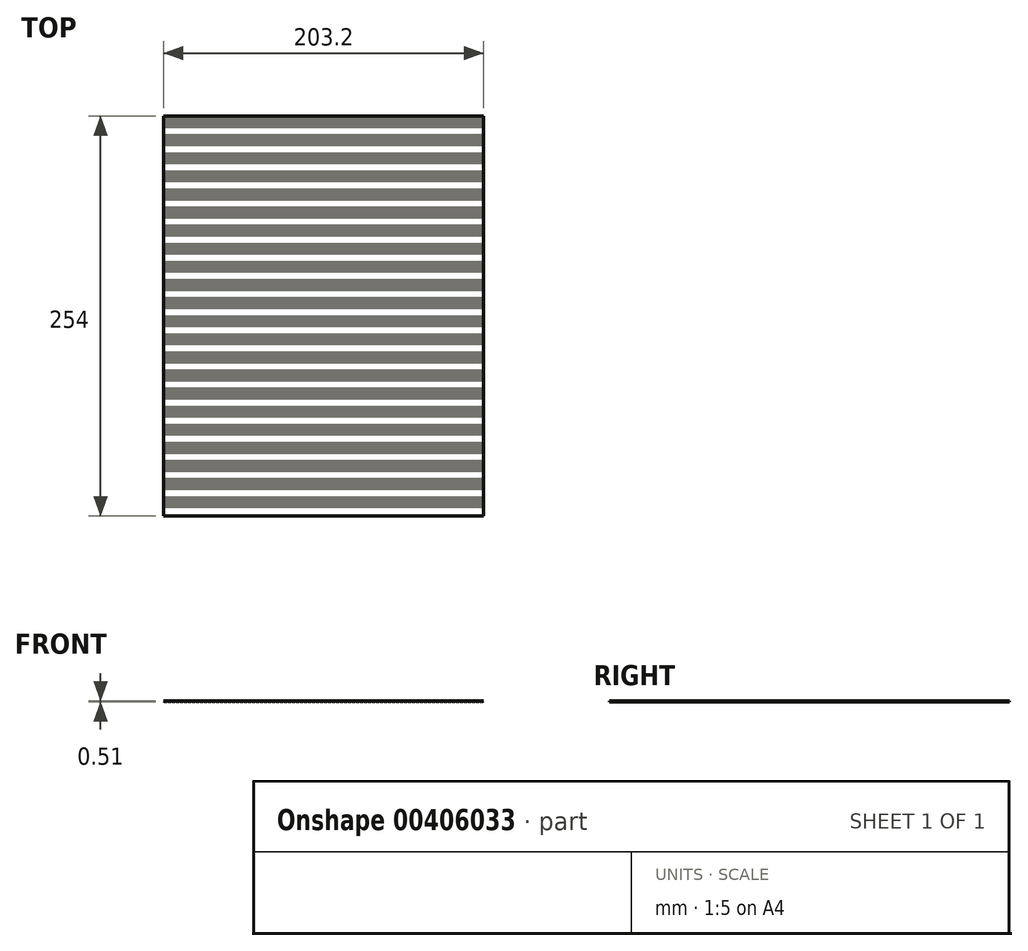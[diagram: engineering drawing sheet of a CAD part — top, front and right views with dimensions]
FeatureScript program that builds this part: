
annotation { "Feature Type Name" : "Feature", "Feature Type Description" : "" }
export const myFeature = defineFeature(function(context is Context, id is Id, definition is map)
    precondition{}
    {
        {
            var Q0;
            Q0=qCreatedBy(makeId("Front.planeOp"),FACE);
            var sketch = newSketch(context, id + "F0", { "sketchPlane" : qUnion([Q0])});
            skLineSegment(sketch, "E0", {"start": v(0, 0) * mm, "end": v(-1.27, -0.5) * mm});
            skLineSegment(sketch, "E1", {"start": v(-1.27, -0.5) * mm, "end": v(-2.54, 0) * mm});
            skLineSegment(sketch, "E2", {"start": v(0, 0) * mm, "end": v(-2.54, 0) * mm, "construction": true});
            skLineSegment(sketch, "E3.1.0.0", {"start": v(-3.8, -0.5) * mm, "end": v(-5.08, 0) * mm});
            skLineSegment(sketch, "E3.1.0.1", {"start": v(-2.54, 0) * mm, "end": v(-3.81, -0.5) * mm});
            skLineSegment(sketch, "E3.1.0.2", {"start": v(-2.54, 0) * mm, "end": v(-5.08, 0) * mm, "construction": true});
            skLineSegment(sketch, "E3.2.0.0", {"start": v(-6.35, -0.5) * mm, "end": v(-7.62, 0) * mm});
            skLineSegment(sketch, "E3.2.0.1", {"start": v(-5.08, 0) * mm, "end": v(-6.35, -0.5) * mm});
            skLineSegment(sketch, "E3.2.0.2", {"start": v(-5.08, 0) * mm, "end": v(-7.62, 0) * mm, "construction": true});
            skLineSegment(sketch, "E3.direction1", {"start": v(-2.54, 0) * mm, "end": v(-5.08, 0) * mm, "construction": true});
            skLineSegment(sketch, "E4.0.3.0", {"start": v(-8.89, -0.5) * mm, "end": v(-10.16, 0) * mm});
            skLineSegment(sketch, "E4.3.3.0", {"start": v(-7.62, 0) * mm, "end": v(-8.89, -0.5) * mm});
            skLineSegment(sketch, "E4.6.3.0", {"start": v(-7.62, 0) * mm, "end": v(-10.16, 0) * mm, "construction": true});
            skLineSegment(sketch, "E4.0.4.0", {"start": v(-11.43, -0.5) * mm, "end": v(-12.7, 0) * mm});
            skLineSegment(sketch, "E4.3.4.0", {"start": v(-10.16, 0) * mm, "end": v(-11.43, -0.5) * mm});
            skLineSegment(sketch, "E4.6.4.0", {"start": v(-10.16, 0) * mm, "end": v(-12.7, 0) * mm, "construction": true});
            skLineSegment(sketch, "E4.0.5.0", {"start": v(-13.97, -0.5) * mm, "end": v(-15.24, 0) * mm});
            skLineSegment(sketch, "E4.3.5.0", {"start": v(-12.7, 0) * mm, "end": v(-13.97, -0.5) * mm});
            skLineSegment(sketch, "E4.6.5.0", {"start": v(-12.7, 0) * mm, "end": v(-15.24, 0) * mm, "construction": true});
            skLineSegment(sketch, "E4.0.6.0", {"start": v(-16.5, -0.5) * mm, "end": v(-17.78, 0) * mm});
            skLineSegment(sketch, "E4.3.6.0", {"start": v(-15.24, 0) * mm, "end": v(-16.5, -0.5) * mm});
            skLineSegment(sketch, "E4.6.6.0", {"start": v(-15.24, 0) * mm, "end": v(-17.78, 0) * mm, "construction": true});
            skLineSegment(sketch, "E4.0.7.0", {"start": v(-19.05, -0.5) * mm, "end": v(-20.32, 0) * mm});
            skLineSegment(sketch, "E4.3.7.0", {"start": v(-17.78, 0) * mm, "end": v(-19.05, -0.5) * mm});
            skLineSegment(sketch, "E4.6.7.0", {"start": v(-17.78, 0) * mm, "end": v(-20.32, 0) * mm, "construction": true});
            skLineSegment(sketch, "E4.0.8.0", {"start": v(-21.59, -0.5) * mm, "end": v(-22.86, 0) * mm});
            skLineSegment(sketch, "E4.3.8.0", {"start": v(-20.32, 0) * mm, "end": v(-21.59, -0.5) * mm});
            skLineSegment(sketch, "E4.6.8.0", {"start": v(-20.32, 0) * mm, "end": v(-22.86, 0) * mm, "construction": true});
            skLineSegment(sketch, "E4.0.9.0", {"start": v(-24.13, -0.5) * mm, "end": v(-25.4, 0) * mm});
            skLineSegment(sketch, "E4.3.9.0", {"start": v(-22.86, 0) * mm, "end": v(-24.13, -0.5) * mm});
            skLineSegment(sketch, "E4.6.9.0", {"start": v(-22.86, 0) * mm, "end": v(-25.4, 0) * mm, "construction": true});
            skLineSegment(sketch, "E4.0.10.0", {"start": v(-26.67, -0.5) * mm, "end": v(-27.94, 0) * mm});
            skLineSegment(sketch, "E4.3.10.0", {"start": v(-25.4, 0) * mm, "end": v(-26.67, -0.5) * mm});
            skLineSegment(sketch, "E4.6.10.0", {"start": v(-25.4, 0) * mm, "end": v(-27.94, 0) * mm, "construction": true});
            skLineSegment(sketch, "E4.0.11.0", {"start": v(-29.2, -0.5) * mm, "end": v(-30.48, 0) * mm});
            skLineSegment(sketch, "E4.3.11.0", {"start": v(-27.94, 0) * mm, "end": v(-29.21, -0.5) * mm});
            skLineSegment(sketch, "E4.6.11.0", {"start": v(-27.94, 0) * mm, "end": v(-30.48, 0) * mm, "construction": true});
            skLineSegment(sketch, "E4.0.12.0", {"start": v(-31.75, -0.5) * mm, "end": v(-33.02, 0) * mm});
            skLineSegment(sketch, "E4.3.12.0", {"start": v(-30.48, 0) * mm, "end": v(-31.75, -0.5) * mm});
            skLineSegment(sketch, "E4.6.12.0", {"start": v(-30.48, 0) * mm, "end": v(-33.02, 0) * mm, "construction": true});
            skLineSegment(sketch, "E4.0.13.0", {"start": v(-34.3, -0.5) * mm, "end": v(-35.56, 0) * mm});
            skLineSegment(sketch, "E4.3.13.0", {"start": v(-33.02, 0) * mm, "end": v(-34.29, -0.5) * mm});
            skLineSegment(sketch, "E4.6.13.0", {"start": v(-33.02, 0) * mm, "end": v(-35.56, 0) * mm, "construction": true});
            skLineSegment(sketch, "E4.0.14.0", {"start": v(-36.83, -0.5) * mm, "end": v(-38.1, 0) * mm});
            skLineSegment(sketch, "E4.3.14.0", {"start": v(-35.56, 0) * mm, "end": v(-36.83, -0.5) * mm});
            skLineSegment(sketch, "E4.6.14.0", {"start": v(-35.56, 0) * mm, "end": v(-38.1, 0) * mm, "construction": true});
            skLineSegment(sketch, "E4.0.15.0", {"start": v(-39.37, -0.5) * mm, "end": v(-40.64, 0) * mm});
            skLineSegment(sketch, "E4.3.15.0", {"start": v(-38.1, 0) * mm, "end": v(-39.37, -0.5) * mm});
            skLineSegment(sketch, "E4.6.15.0", {"start": v(-38.1, 0) * mm, "end": v(-40.64, 0) * mm, "construction": true});
            skLineSegment(sketch, "E4.0.16.0", {"start": v(-41.9, -0.5) * mm, "end": v(-43.18, 0) * mm});
            skLineSegment(sketch, "E4.3.16.0", {"start": v(-40.64, 0) * mm, "end": v(-41.9, -0.5) * mm});
            skLineSegment(sketch, "E4.6.16.0", {"start": v(-40.64, 0) * mm, "end": v(-43.18, 0) * mm, "construction": true});
            skLineSegment(sketch, "E4.0.17.0", {"start": v(-44.45, -0.5) * mm, "end": v(-45.72, 0) * mm});
            skLineSegment(sketch, "E4.3.17.0", {"start": v(-43.18, 0) * mm, "end": v(-44.45, -0.5) * mm});
            skLineSegment(sketch, "E4.6.17.0", {"start": v(-43.18, 0) * mm, "end": v(-45.72, 0) * mm, "construction": true});
            skLineSegment(sketch, "E4.0.18.0", {"start": v(-46.99, -0.5) * mm, "end": v(-48.26, 0) * mm});
            skLineSegment(sketch, "E4.3.18.0", {"start": v(-45.72, 0) * mm, "end": v(-46.99, -0.5) * mm});
            skLineSegment(sketch, "E4.6.18.0", {"start": v(-45.72, 0) * mm, "end": v(-48.26, 0) * mm, "construction": true});
            skLineSegment(sketch, "E4.0.19.0", {"start": v(-49.53, -0.5) * mm, "end": v(-50.8, 0) * mm});
            skLineSegment(sketch, "E4.3.19.0", {"start": v(-48.26, 0) * mm, "end": v(-49.53, -0.5) * mm});
            skLineSegment(sketch, "E4.6.19.0", {"start": v(-48.26, 0) * mm, "end": v(-50.8, 0) * mm, "construction": true});
            skLineSegment(sketch, "E4.0.20.0", {"start": v(-52.07, -0.5) * mm, "end": v(-53.34, 0) * mm});
            skLineSegment(sketch, "E4.3.20.0", {"start": v(-50.8, 0) * mm, "end": v(-52.07, -0.5) * mm});
            skLineSegment(sketch, "E4.6.20.0", {"start": v(-50.8, 0) * mm, "end": v(-53.34, 0) * mm, "construction": true});
            skLineSegment(sketch, "E4.0.21.0", {"start": v(-54.6, -0.5) * mm, "end": v(-55.88, 0) * mm});
            skLineSegment(sketch, "E4.3.21.0", {"start": v(-53.34, 0) * mm, "end": v(-54.61, -0.5) * mm});
            skLineSegment(sketch, "E4.6.21.0", {"start": v(-53.34, 0) * mm, "end": v(-55.88, 0) * mm, "construction": true});
            skLineSegment(sketch, "E4.0.22.0", {"start": v(-57.15, -0.5) * mm, "end": v(-58.42, 0) * mm});
            skLineSegment(sketch, "E4.3.22.0", {"start": v(-55.88, 0) * mm, "end": v(-57.15, -0.5) * mm});
            skLineSegment(sketch, "E4.6.22.0", {"start": v(-55.88, 0) * mm, "end": v(-58.42, 0) * mm, "construction": true});
            skLineSegment(sketch, "E4.0.23.0", {"start": v(-59.69, -0.5) * mm, "end": v(-60.96, 0) * mm});
            skLineSegment(sketch, "E4.3.23.0", {"start": v(-58.42, 0) * mm, "end": v(-59.69, -0.5) * mm});
            skLineSegment(sketch, "E4.6.23.0", {"start": v(-58.42, 0) * mm, "end": v(-60.96, 0) * mm, "construction": true});
            skLineSegment(sketch, "E4.0.24.0", {"start": v(-62.23, -0.5) * mm, "end": v(-63.5, 0) * mm});
            skLineSegment(sketch, "E4.3.24.0", {"start": v(-60.96, 0) * mm, "end": v(-62.23, -0.5) * mm});
            skLineSegment(sketch, "E4.6.24.0", {"start": v(-60.96, 0) * mm, "end": v(-63.5, 0) * mm, "construction": true});
            skLineSegment(sketch, "E4.0.25.0", {"start": v(-64.77, -0.5) * mm, "end": v(-66.04, 0) * mm});
            skLineSegment(sketch, "E4.3.25.0", {"start": v(-63.5, 0) * mm, "end": v(-64.77, -0.5) * mm});
            skLineSegment(sketch, "E4.6.25.0", {"start": v(-63.5, 0) * mm, "end": v(-66.04, 0) * mm, "construction": true});
            skLineSegment(sketch, "E4.0.26.0", {"start": v(-67.31, -0.5) * mm, "end": v(-68.58, 0) * mm});
            skLineSegment(sketch, "E4.3.26.0", {"start": v(-66.04, 0) * mm, "end": v(-67.3, -0.5) * mm});
            skLineSegment(sketch, "E4.6.26.0", {"start": v(-66.04, 0) * mm, "end": v(-68.58, 0) * mm, "construction": true});
            skLineSegment(sketch, "E4.0.27.0", {"start": v(-69.85, -0.5) * mm, "end": v(-71.12, 0) * mm});
            skLineSegment(sketch, "E4.3.27.0", {"start": v(-68.58, 0) * mm, "end": v(-69.85, -0.5) * mm});
            skLineSegment(sketch, "E4.6.27.0", {"start": v(-68.58, 0) * mm, "end": v(-71.12, 0) * mm, "construction": true});
            skLineSegment(sketch, "E4.0.28.0", {"start": v(-72.39, -0.5) * mm, "end": v(-73.66, 0) * mm});
            skLineSegment(sketch, "E4.3.28.0", {"start": v(-71.12, 0) * mm, "end": v(-72.39, -0.5) * mm});
            skLineSegment(sketch, "E4.6.28.0", {"start": v(-71.12, 0) * mm, "end": v(-73.66, 0) * mm, "construction": true});
            skLineSegment(sketch, "E4.0.29.0", {"start": v(-74.93, -0.5) * mm, "end": v(-76.2, 0) * mm});
            skLineSegment(sketch, "E4.3.29.0", {"start": v(-73.66, 0) * mm, "end": v(-74.93, -0.5) * mm});
            skLineSegment(sketch, "E4.6.29.0", {"start": v(-73.66, 0) * mm, "end": v(-76.2, 0) * mm, "construction": true});
            skLineSegment(sketch, "E4.0.30.0", {"start": v(-77.47, -0.5) * mm, "end": v(-78.74, 0) * mm});
            skLineSegment(sketch, "E4.3.30.0", {"start": v(-76.2, 0) * mm, "end": v(-77.47, -0.5) * mm});
            skLineSegment(sketch, "E4.6.30.0", {"start": v(-76.2, 0) * mm, "end": v(-78.74, 0) * mm, "construction": true});
            skLineSegment(sketch, "E4.0.31.0", {"start": v(-80, -0.5) * mm, "end": v(-81.28, 0) * mm});
            skLineSegment(sketch, "E4.3.31.0", {"start": v(-78.74, 0) * mm, "end": v(-80, -0.5) * mm});
            skLineSegment(sketch, "E4.6.31.0", {"start": v(-78.74, 0) * mm, "end": v(-81.28, 0) * mm, "construction": true});
            skLineSegment(sketch, "E4.0.32.0", {"start": v(-82.55, -0.5) * mm, "end": v(-83.82, 0) * mm});
            skLineSegment(sketch, "E4.3.32.0", {"start": v(-81.28, 0) * mm, "end": v(-82.55, -0.5) * mm});
            skLineSegment(sketch, "E4.6.32.0", {"start": v(-81.28, 0) * mm, "end": v(-83.82, 0) * mm, "construction": true});
            skLineSegment(sketch, "E4.0.33.0", {"start": v(-85.1, -0.5) * mm, "end": v(-86.36, 0) * mm});
            skLineSegment(sketch, "E4.3.33.0", {"start": v(-83.82, 0) * mm, "end": v(-85.1, -0.5) * mm});
            skLineSegment(sketch, "E4.6.33.0", {"start": v(-83.82, 0) * mm, "end": v(-86.36, 0) * mm, "construction": true});
            skLineSegment(sketch, "E4.0.34.0", {"start": v(-87.63, -0.5) * mm, "end": v(-88.9, 0) * mm});
            skLineSegment(sketch, "E4.3.34.0", {"start": v(-86.36, 0) * mm, "end": v(-87.63, -0.5) * mm});
            skLineSegment(sketch, "E4.6.34.0", {"start": v(-86.36, 0) * mm, "end": v(-88.9, 0) * mm, "construction": true});
            skLineSegment(sketch, "E4.0.35.0", {"start": v(-90.17, -0.5) * mm, "end": v(-91.44, 0) * mm});
            skLineSegment(sketch, "E4.3.35.0", {"start": v(-88.9, 0) * mm, "end": v(-90.17, -0.5) * mm});
            skLineSegment(sketch, "E4.6.35.0", {"start": v(-88.9, 0) * mm, "end": v(-91.44, 0) * mm, "construction": true});
            skLineSegment(sketch, "E4.0.36.0", {"start": v(-92.7, -0.5) * mm, "end": v(-93.98, 0) * mm});
            skLineSegment(sketch, "E4.3.36.0", {"start": v(-91.44, 0) * mm, "end": v(-92.7, -0.5) * mm});
            skLineSegment(sketch, "E4.6.36.0", {"start": v(-91.44, 0) * mm, "end": v(-93.98, 0) * mm, "construction": true});
            skLineSegment(sketch, "E4.0.37.0", {"start": v(-95.25, -0.5) * mm, "end": v(-96.52, 0) * mm});
            skLineSegment(sketch, "E4.3.37.0", {"start": v(-93.98, 0) * mm, "end": v(-95.25, -0.5) * mm});
            skLineSegment(sketch, "E4.6.37.0", {"start": v(-93.98, 0) * mm, "end": v(-96.52, 0) * mm, "construction": true});
            skLineSegment(sketch, "E4.0.38.0", {"start": v(-97.79, -0.5) * mm, "end": v(-99.06, 0) * mm});
            skLineSegment(sketch, "E4.3.38.0", {"start": v(-96.52, 0) * mm, "end": v(-97.8, -0.5) * mm});
            skLineSegment(sketch, "E4.6.38.0", {"start": v(-96.52, 0) * mm, "end": v(-99.06, 0) * mm, "construction": true});
            skLineSegment(sketch, "E4.0.39.0", {"start": v(-100.33, -0.5) * mm, "end": v(-101.6, 0) * mm});
            skLineSegment(sketch, "E4.3.39.0", {"start": v(-99.06, 0) * mm, "end": v(-100.33, -0.5) * mm});
            skLineSegment(sketch, "E4.6.39.0", {"start": v(-99.06, 0) * mm, "end": v(-101.6, 0) * mm, "construction": true});
            skLineSegment(sketch, "E5", {"start": v(0, 0) * mm, "end": v(0, 0) * mm});
            skLineSegment(sketch, "E6", {"start": v(0, 0) * mm, "end": v(-203.2, 0) * mm});
            skLineSegment(sketch, "E7.0.40.0", {"start": v(-102.87, -0.5) * mm, "end": v(-104.14, 0) * mm});
            skLineSegment(sketch, "E7.3.40.0", {"start": v(-101.6, 0) * mm, "end": v(-102.87, -0.5) * mm});
            skLineSegment(sketch, "E7.6.40.0", {"start": v(-101.6, 0) * mm, "end": v(-104.14, 0) * mm, "construction": true});
            skLineSegment(sketch, "E7.0.41.0", {"start": v(-105.41, -0.5) * mm, "end": v(-106.68, 0) * mm});
            skLineSegment(sketch, "E7.3.41.0", {"start": v(-104.14, 0) * mm, "end": v(-105.41, -0.5) * mm});
            skLineSegment(sketch, "E7.6.41.0", {"start": v(-104.14, 0) * mm, "end": v(-106.68, 0) * mm, "construction": true});
            skLineSegment(sketch, "E7.0.42.0", {"start": v(-107.95, -0.5) * mm, "end": v(-109.22, 0) * mm});
            skLineSegment(sketch, "E7.3.42.0", {"start": v(-106.68, 0) * mm, "end": v(-107.95, -0.5) * mm});
            skLineSegment(sketch, "E7.6.42.0", {"start": v(-106.68, 0) * mm, "end": v(-109.22, 0) * mm, "construction": true});
            skLineSegment(sketch, "E7.0.43.0", {"start": v(-110.5, -0.5) * mm, "end": v(-111.76, 0) * mm});
            skLineSegment(sketch, "E7.3.43.0", {"start": v(-109.22, 0) * mm, "end": v(-110.5, -0.5) * mm});
            skLineSegment(sketch, "E7.6.43.0", {"start": v(-109.22, 0) * mm, "end": v(-111.76, 0) * mm, "construction": true});
            skLineSegment(sketch, "E7.0.44.0", {"start": v(-113.03, -0.5) * mm, "end": v(-114.3, 0) * mm});
            skLineSegment(sketch, "E7.3.44.0", {"start": v(-111.76, 0) * mm, "end": v(-113.03, -0.5) * mm});
            skLineSegment(sketch, "E7.6.44.0", {"start": v(-111.76, 0) * mm, "end": v(-114.3, 0) * mm, "construction": true});
            skLineSegment(sketch, "E7.0.45.0", {"start": v(-115.57, -0.5) * mm, "end": v(-116.84, 0) * mm});
            skLineSegment(sketch, "E7.3.45.0", {"start": v(-114.3, 0) * mm, "end": v(-115.57, -0.5) * mm});
            skLineSegment(sketch, "E7.6.45.0", {"start": v(-114.3, 0) * mm, "end": v(-116.84, 0) * mm, "construction": true});
            skLineSegment(sketch, "E7.0.46.0", {"start": v(-118.11, -0.5) * mm, "end": v(-119.38, 0) * mm});
            skLineSegment(sketch, "E7.3.46.0", {"start": v(-116.84, 0) * mm, "end": v(-118.11, -0.5) * mm});
            skLineSegment(sketch, "E7.6.46.0", {"start": v(-116.84, 0) * mm, "end": v(-119.38, 0) * mm, "construction": true});
            skLineSegment(sketch, "E7.0.47.0", {"start": v(-120.65, -0.5) * mm, "end": v(-121.92, 0) * mm});
            skLineSegment(sketch, "E7.3.47.0", {"start": v(-119.38, 0) * mm, "end": v(-120.65, -0.5) * mm});
            skLineSegment(sketch, "E7.6.47.0", {"start": v(-119.38, 0) * mm, "end": v(-121.92, 0) * mm, "construction": true});
            skLineSegment(sketch, "E7.0.48.0", {"start": v(-123.2, -0.5) * mm, "end": v(-124.46, 0) * mm});
            skLineSegment(sketch, "E7.3.48.0", {"start": v(-121.92, 0) * mm, "end": v(-123.19, -0.5) * mm});
            skLineSegment(sketch, "E7.6.48.0", {"start": v(-121.92, 0) * mm, "end": v(-124.46, 0) * mm, "construction": true});
            skLineSegment(sketch, "E7.0.49.0", {"start": v(-125.73, -0.5) * mm, "end": v(-127, 0) * mm});
            skLineSegment(sketch, "E7.3.49.0", {"start": v(-124.46, 0) * mm, "end": v(-125.73, -0.5) * mm});
            skLineSegment(sketch, "E7.6.49.0", {"start": v(-124.46, 0) * mm, "end": v(-127, 0) * mm, "construction": true});
            skLineSegment(sketch, "E7.0.50.0", {"start": v(-128.27, -0.5) * mm, "end": v(-129.54, 0) * mm});
            skLineSegment(sketch, "E7.3.50.0", {"start": v(-127, 0) * mm, "end": v(-128.27, -0.5) * mm});
            skLineSegment(sketch, "E7.6.50.0", {"start": v(-127, 0) * mm, "end": v(-129.54, 0) * mm, "construction": true});
            skLineSegment(sketch, "E7.0.51.0", {"start": v(-130.81, -0.5) * mm, "end": v(-132.08, 0) * mm});
            skLineSegment(sketch, "E7.3.51.0", {"start": v(-129.54, 0) * mm, "end": v(-130.81, -0.5) * mm});
            skLineSegment(sketch, "E7.6.51.0", {"start": v(-129.54, 0) * mm, "end": v(-132.08, 0) * mm, "construction": true});
            skLineSegment(sketch, "E7.0.52.0", {"start": v(-133.35, -0.5) * mm, "end": v(-134.62, 0) * mm});
            skLineSegment(sketch, "E7.3.52.0", {"start": v(-132.08, 0) * mm, "end": v(-133.35, -0.5) * mm});
            skLineSegment(sketch, "E7.6.52.0", {"start": v(-132.08, 0) * mm, "end": v(-134.62, 0) * mm, "construction": true});
            skLineSegment(sketch, "E7.0.53.0", {"start": v(-135.9, -0.5) * mm, "end": v(-137.16, 0) * mm});
            skLineSegment(sketch, "E7.3.53.0", {"start": v(-134.62, 0) * mm, "end": v(-135.89, -0.5) * mm});
            skLineSegment(sketch, "E7.6.53.0", {"start": v(-134.62, 0) * mm, "end": v(-137.16, 0) * mm, "construction": true});
            skLineSegment(sketch, "E7.0.54.0", {"start": v(-138.43, -0.5) * mm, "end": v(-139.7, 0) * mm});
            skLineSegment(sketch, "E7.3.54.0", {"start": v(-137.16, 0) * mm, "end": v(-138.43, -0.5) * mm});
            skLineSegment(sketch, "E7.6.54.0", {"start": v(-137.16, 0) * mm, "end": v(-139.7, 0) * mm, "construction": true});
            skLineSegment(sketch, "E7.0.55.0", {"start": v(-140.97, -0.5) * mm, "end": v(-142.24, 0) * mm});
            skLineSegment(sketch, "E7.3.55.0", {"start": v(-139.7, 0) * mm, "end": v(-140.97, -0.5) * mm});
            skLineSegment(sketch, "E7.6.55.0", {"start": v(-139.7, 0) * mm, "end": v(-142.24, 0) * mm, "construction": true});
            skLineSegment(sketch, "E7.0.56.0", {"start": v(-143.51, -0.5) * mm, "end": v(-144.78, 0) * mm});
            skLineSegment(sketch, "E7.3.56.0", {"start": v(-142.24, 0) * mm, "end": v(-143.51, -0.5) * mm});
            skLineSegment(sketch, "E7.6.56.0", {"start": v(-142.24, 0) * mm, "end": v(-144.78, 0) * mm, "construction": true});
            skLineSegment(sketch, "E7.0.57.0", {"start": v(-146.05, -0.5) * mm, "end": v(-147.32, 0) * mm});
            skLineSegment(sketch, "E7.3.57.0", {"start": v(-144.78, 0) * mm, "end": v(-146.05, -0.5) * mm});
            skLineSegment(sketch, "E7.6.57.0", {"start": v(-144.78, 0) * mm, "end": v(-147.32, 0) * mm, "construction": true});
            skLineSegment(sketch, "E7.0.58.0", {"start": v(-148.6, -0.5) * mm, "end": v(-149.86, 0) * mm});
            skLineSegment(sketch, "E7.3.58.0", {"start": v(-147.32, 0) * mm, "end": v(-148.6, -0.5) * mm});
            skLineSegment(sketch, "E7.6.58.0", {"start": v(-147.32, 0) * mm, "end": v(-149.86, 0) * mm, "construction": true});
            skLineSegment(sketch, "E7.0.59.0", {"start": v(-151.13, -0.5) * mm, "end": v(-152.4, 0) * mm});
            skLineSegment(sketch, "E7.3.59.0", {"start": v(-149.86, 0) * mm, "end": v(-151.13, -0.5) * mm});
            skLineSegment(sketch, "E7.6.59.0", {"start": v(-149.86, 0) * mm, "end": v(-152.4, 0) * mm, "construction": true});
            skLineSegment(sketch, "E7.0.60.0", {"start": v(-153.67, -0.5) * mm, "end": v(-154.94, 0) * mm});
            skLineSegment(sketch, "E7.3.60.0", {"start": v(-152.4, 0) * mm, "end": v(-153.67, -0.5) * mm});
            skLineSegment(sketch, "E7.6.60.0", {"start": v(-152.4, 0) * mm, "end": v(-154.94, 0) * mm, "construction": true});
            skLineSegment(sketch, "E7.0.61.0", {"start": v(-156.21, -0.5) * mm, "end": v(-157.48, 0) * mm});
            skLineSegment(sketch, "E7.3.61.0", {"start": v(-154.94, 0) * mm, "end": v(-156.21, -0.5) * mm});
            skLineSegment(sketch, "E7.6.61.0", {"start": v(-154.94, 0) * mm, "end": v(-157.48, 0) * mm, "construction": true});
            skLineSegment(sketch, "E7.0.62.0", {"start": v(-158.75, -0.5) * mm, "end": v(-160.02, 0) * mm});
            skLineSegment(sketch, "E7.3.62.0", {"start": v(-157.48, 0) * mm, "end": v(-158.75, -0.5) * mm});
            skLineSegment(sketch, "E7.6.62.0", {"start": v(-157.48, 0) * mm, "end": v(-160.02, 0) * mm, "construction": true});
            skLineSegment(sketch, "E7.0.63.0", {"start": v(-161.3, -0.5) * mm, "end": v(-162.56, 0) * mm});
            skLineSegment(sketch, "E7.3.63.0", {"start": v(-160.02, 0) * mm, "end": v(-161.29, -0.5) * mm});
            skLineSegment(sketch, "E7.6.63.0", {"start": v(-160.02, 0) * mm, "end": v(-162.56, 0) * mm, "construction": true});
            skLineSegment(sketch, "E7.0.64.0", {"start": v(-163.83, -0.5) * mm, "end": v(-165.1, 0) * mm});
            skLineSegment(sketch, "E7.3.64.0", {"start": v(-162.56, 0) * mm, "end": v(-163.83, -0.5) * mm});
            skLineSegment(sketch, "E7.6.64.0", {"start": v(-162.56, 0) * mm, "end": v(-165.1, 0) * mm, "construction": true});
            skLineSegment(sketch, "E7.0.65.0", {"start": v(-166.37, -0.5) * mm, "end": v(-167.64, 0) * mm});
            skLineSegment(sketch, "E7.3.65.0", {"start": v(-165.1, 0) * mm, "end": v(-166.37, -0.5) * mm});
            skLineSegment(sketch, "E7.6.65.0", {"start": v(-165.1, 0) * mm, "end": v(-167.64, 0) * mm, "construction": true});
            skLineSegment(sketch, "E7.0.66.0", {"start": v(-168.9, -0.5) * mm, "end": v(-170.18, 0) * mm});
            skLineSegment(sketch, "E7.3.66.0", {"start": v(-167.64, 0) * mm, "end": v(-168.9, -0.5) * mm});
            skLineSegment(sketch, "E7.6.66.0", {"start": v(-167.64, 0) * mm, "end": v(-170.18, 0) * mm, "construction": true});
            skLineSegment(sketch, "E7.0.67.0", {"start": v(-171.45, -0.5) * mm, "end": v(-172.72, 0) * mm});
            skLineSegment(sketch, "E7.3.67.0", {"start": v(-170.18, 0) * mm, "end": v(-171.45, -0.5) * mm});
            skLineSegment(sketch, "E7.6.67.0", {"start": v(-170.18, 0) * mm, "end": v(-172.72, 0) * mm, "construction": true});
            skLineSegment(sketch, "E7.0.68.0", {"start": v(-174, -0.5) * mm, "end": v(-175.26, 0) * mm});
            skLineSegment(sketch, "E7.3.68.0", {"start": v(-172.72, 0) * mm, "end": v(-173.99, -0.5) * mm});
            skLineSegment(sketch, "E7.6.68.0", {"start": v(-172.72, 0) * mm, "end": v(-175.26, 0) * mm, "construction": true});
            skLineSegment(sketch, "E7.0.69.0", {"start": v(-176.53, -0.5) * mm, "end": v(-177.8, 0) * mm});
            skLineSegment(sketch, "E7.3.69.0", {"start": v(-175.26, 0) * mm, "end": v(-176.53, -0.5) * mm});
            skLineSegment(sketch, "E7.6.69.0", {"start": v(-175.26, 0) * mm, "end": v(-177.8, 0) * mm, "construction": true});
            skLineSegment(sketch, "E7.0.70.0", {"start": v(-179.07, -0.5) * mm, "end": v(-180.34, 0) * mm});
            skLineSegment(sketch, "E7.3.70.0", {"start": v(-177.8, 0) * mm, "end": v(-179.07, -0.5) * mm});
            skLineSegment(sketch, "E7.6.70.0", {"start": v(-177.8, 0) * mm, "end": v(-180.34, 0) * mm, "construction": true});
            skLineSegment(sketch, "E7.0.71.0", {"start": v(-181.61, -0.5) * mm, "end": v(-182.88, 0) * mm});
            skLineSegment(sketch, "E7.3.71.0", {"start": v(-180.34, 0) * mm, "end": v(-181.6, -0.5) * mm});
            skLineSegment(sketch, "E7.6.71.0", {"start": v(-180.34, 0) * mm, "end": v(-182.88, 0) * mm, "construction": true});
            skLineSegment(sketch, "E7.0.72.0", {"start": v(-184.15, -0.5) * mm, "end": v(-185.42, 0) * mm});
            skLineSegment(sketch, "E7.3.72.0", {"start": v(-182.88, 0) * mm, "end": v(-184.15, -0.5) * mm});
            skLineSegment(sketch, "E7.6.72.0", {"start": v(-182.88, 0) * mm, "end": v(-185.42, 0) * mm, "construction": true});
            skLineSegment(sketch, "E7.0.73.0", {"start": v(-186.7, -0.5) * mm, "end": v(-187.96, 0) * mm});
            skLineSegment(sketch, "E7.3.73.0", {"start": v(-185.42, 0) * mm, "end": v(-186.69, -0.5) * mm});
            skLineSegment(sketch, "E7.6.73.0", {"start": v(-185.42, 0) * mm, "end": v(-187.96, 0) * mm, "construction": true});
            skLineSegment(sketch, "E7.0.74.0", {"start": v(-189.23, -0.5) * mm, "end": v(-190.5, 0) * mm});
            skLineSegment(sketch, "E7.3.74.0", {"start": v(-187.96, 0) * mm, "end": v(-189.23, -0.5) * mm});
            skLineSegment(sketch, "E7.6.74.0", {"start": v(-187.96, 0) * mm, "end": v(-190.5, 0) * mm, "construction": true});
            skLineSegment(sketch, "E7.0.75.0", {"start": v(-191.77, -0.5) * mm, "end": v(-193.04, 0) * mm});
            skLineSegment(sketch, "E7.3.75.0", {"start": v(-190.5, 0) * mm, "end": v(-191.77, -0.5) * mm});
            skLineSegment(sketch, "E7.6.75.0", {"start": v(-190.5, 0) * mm, "end": v(-193.04, 0) * mm, "construction": true});
            skLineSegment(sketch, "E7.0.76.0", {"start": v(-194.31, -0.5) * mm, "end": v(-195.58, 0) * mm});
            skLineSegment(sketch, "E7.3.76.0", {"start": v(-193.04, 0) * mm, "end": v(-194.3, -0.5) * mm});
            skLineSegment(sketch, "E7.6.76.0", {"start": v(-193.04, 0) * mm, "end": v(-195.58, 0) * mm, "construction": true});
            skLineSegment(sketch, "E7.0.77.0", {"start": v(-196.85, -0.5) * mm, "end": v(-198.12, 0) * mm});
            skLineSegment(sketch, "E7.3.77.0", {"start": v(-195.58, 0) * mm, "end": v(-196.85, -0.5) * mm});
            skLineSegment(sketch, "E7.6.77.0", {"start": v(-195.58, 0) * mm, "end": v(-198.12, 0) * mm, "construction": true});
            skLineSegment(sketch, "E7.0.78.0", {"start": v(-199.4, -0.5) * mm, "end": v(-200.66, 0) * mm});
            skLineSegment(sketch, "E7.3.78.0", {"start": v(-198.12, 0) * mm, "end": v(-199.4, -0.5) * mm});
            skLineSegment(sketch, "E7.6.78.0", {"start": v(-198.12, 0) * mm, "end": v(-200.66, 0) * mm, "construction": true});
            skLineSegment(sketch, "E7.0.79.0", {"start": v(-201.93, -0.5) * mm, "end": v(-203.2, 0) * mm});
            skLineSegment(sketch, "E7.3.79.0", {"start": v(-200.66, 0) * mm, "end": v(-201.93, -0.5) * mm});
            skLineSegment(sketch, "E7.6.79.0", {"start": v(-200.66, 0) * mm, "end": v(-203.2, 0) * mm, "construction": true});
            skLineSegment(sketch, "E8", {"start": v(-203.2, 0) * mm, "end": v(-203.2, 0) * mm});
            skSolve(sketch);
        }
        {
            var Q0;
            Q0=qSketchRegion(id+"F0",true);
            extrude(context, id + "F1", {"entities" : qUnion([Q0]), "oppositeDirection" : true, "depth" : 254 * mm});
        }
    });
